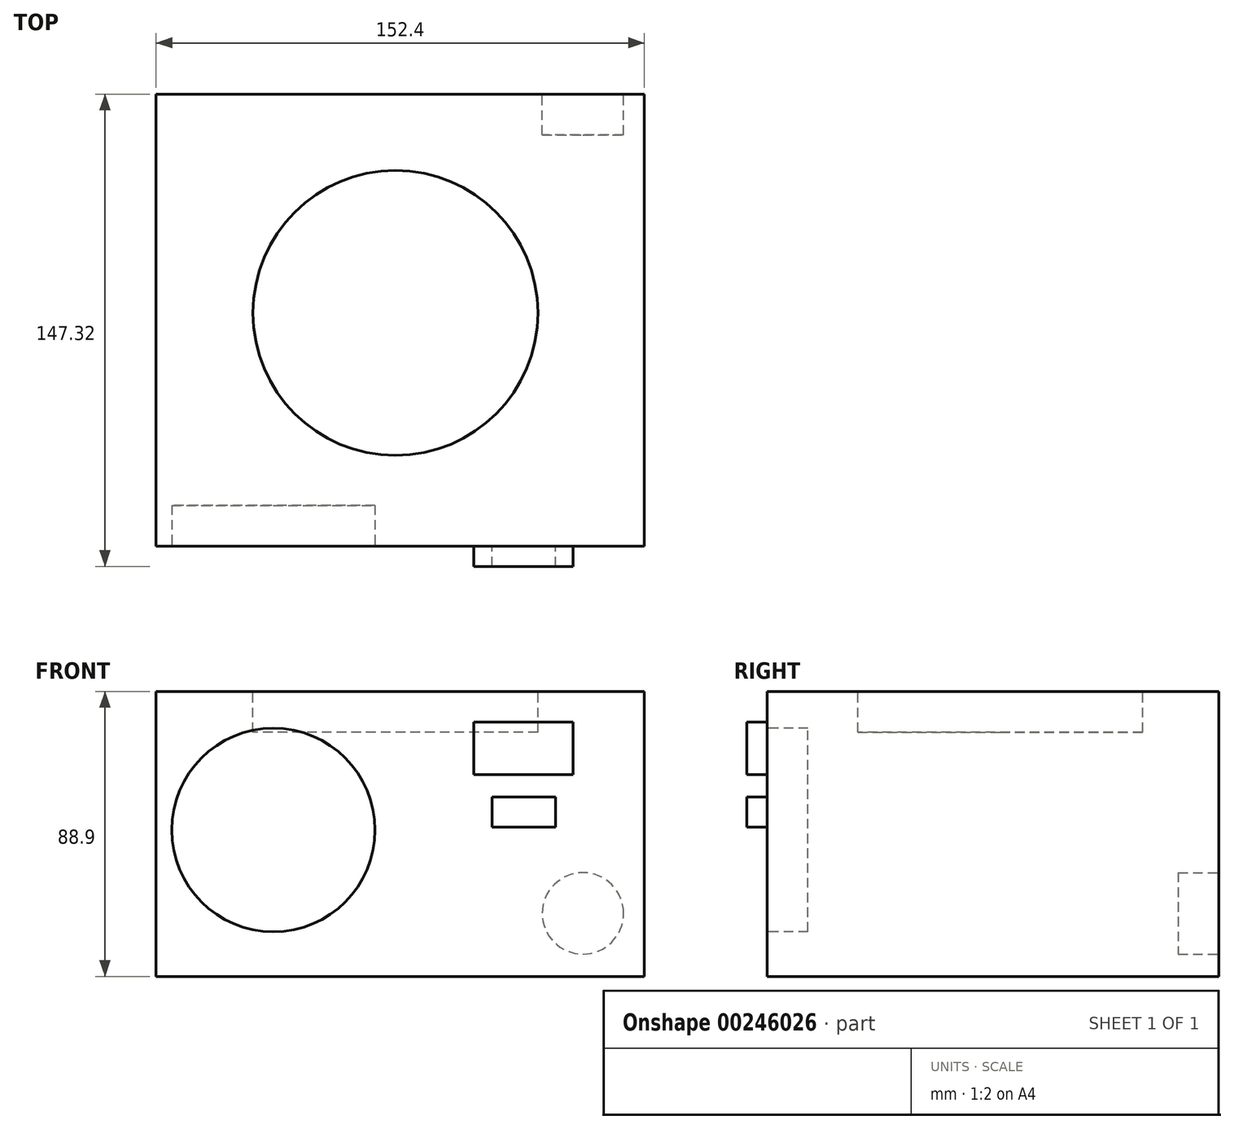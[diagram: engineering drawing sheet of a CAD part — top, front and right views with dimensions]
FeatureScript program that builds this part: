
annotation { "Feature Type Name" : "Feature", "Feature Type Description" : "" }
export const myFeature = defineFeature(function(context is Context, id is Id, definition is map)
    precondition{}
    {
        {
            var Q0;
            Q0=qCreatedBy(makeId("Front.planeOp"),FACE);
            var sketch = newSketch(context, id + "F0", { "sketchPlane" : qUnion([Q0])});
            skLineSegment(sketch, "E0.bottom", {"start": v(0, 0) * mm, "end": v(152.4, 0) * mm});
            skLineSegment(sketch, "E0.top", {"start": v(0, 88.9) * mm, "end": v(152.4, 88.9) * mm});
            skLineSegment(sketch, "E0.left", {"start": v(0, 0) * mm, "end": v(0, 88.9) * mm});
            skLineSegment(sketch, "E0.right", {"start": v(152.4, 0) * mm, "end": v(152.4, 88.9) * mm});
            skSolve(sketch);
        }
        {
            var Q0;
            Q0=makeQuery(id+"F0.imprint","IMPRINT",FACE,{"disambiguationData":[TD([[makeQuery(id+"F0.imprint","IMPRINT",EDGE,{"derivedFrom":sQuery(id+"F0.wireOp",EDGE,"E0.bottom")}),1.0]])]});
            extrude(context, id + "F1", {"entities" : qUnion([Q0]), "oppositeDirection" : true, "depth" : 140.97 * mm});
        }
        {
            var Q0;
            Q0=makeQuery(id+"F1.opExtrude","CAP_FACE",FACE,{"disambiguationData":[OSD([sQuery(id+"F0.wireOp",EDGE,"E0.bottom"),sQuery(id+"F0.wireOp",EDGE,"E0.top"),sQuery(id+"F0.wireOp",EDGE,"E0.left"),sQuery(id+"F0.wireOp",EDGE,"E0.right")])],"isStart":false});
            var sketch = newSketch(context, id + "F2", { "sketchPlane" : qUnion([Q0])});
            skCircle(sketch, "E1", {"center": v(-133.2, 19.65) * mm, "radius": 12.7 * mm});
            skSolve(sketch);
        }
        {
            var Q0;
            Q0=makeQuery(id+"F2.imprint","IMPRINT",FACE,{"disambiguationData":[TD([[makeQuery(id+"F2.imprint","IMPRINT",EDGE,{"derivedFrom":sQuery(id+"F2.wireOp",EDGE,"E1")}),1.0]])]});
            extrude(context, id + "F3", {"entities" : qUnion([Q0]), "operationType" : NewBodyOperationType.REMOVE, "oppositeDirection" : true, "depth" : 12.7 * mm});
        }
        {
            var Q0;
            Q0=makeQuery(id+"F1.opExtrude","SWEPT_FACE",FACE,{"disambiguationData":[OSD([sQuery(id+"F0.wireOp",EDGE,"E0.top")])]});
            var sketch = newSketch(context, id + "F4", { "sketchPlane" : qUnion([Q0])});
            skCircle(sketch, "E2", {"center": v(74.68, 72.68) * mm, "radius": 44.45 * mm});
            skSolve(sketch);
        }
        {
            var Q0;
            Q0=makeQuery(id+"F4.imprint","IMPRINT",FACE,{"disambiguationData":[TD([[makeQuery(id+"F4.imprint","IMPRINT",EDGE,{"derivedFrom":sQuery(id+"F4.wireOp",EDGE,"E2")}),1.0]])]});
            extrude(context, id + "F5", {"entities" : qUnion([Q0]), "operationType" : NewBodyOperationType.REMOVE, "oppositeDirection" : true, "depth" : 12.7 * mm});
        }
        {
            var Q0;
            Q0=makeQuery(id+"F1.opExtrude","CAP_FACE",FACE,{"disambiguationData":[OSD([sQuery(id+"F0.wireOp",EDGE,"E0.bottom"),sQuery(id+"F0.wireOp",EDGE,"E0.top"),sQuery(id+"F0.wireOp",EDGE,"E0.left"),sQuery(id+"F0.wireOp",EDGE,"E0.right")])],"isStart":true});
            var sketch = newSketch(context, id + "F6", { "sketchPlane" : qUnion([Q0])});
            skCircle(sketch, "E3", {"center": v(36.58, 45.67) * mm, "radius": 31.75 * mm});
            skLineSegment(sketch, "E4.bottom", {"start": v(99.12, 79.37) * mm, "end": v(130.1, 79.37) * mm});
            skLineSegment(sketch, "E4.top", {"start": v(99.12, 62.97) * mm, "end": v(130.1, 62.97) * mm});
            skLineSegment(sketch, "E4.left", {"start": v(99.12, 79.37) * mm, "end": v(99.12, 62.97) * mm});
            skLineSegment(sketch, "E4.right", {"start": v(130.1, 79.37) * mm, "end": v(130.1, 62.97) * mm});
            skLineSegment(sketch, "E5.bottom", {"start": v(104.9, 55.99) * mm, "end": v(124.63, 55.99) * mm});
            skLineSegment(sketch, "E5.top", {"start": v(104.9, 46.58) * mm, "end": v(124.63, 46.58) * mm});
            skLineSegment(sketch, "E5.left", {"start": v(104.9, 55.99) * mm, "end": v(104.9, 46.58) * mm});
            skLineSegment(sketch, "E5.right", {"start": v(124.63, 55.99) * mm, "end": v(124.63, 46.58) * mm});
            skSolve(sketch);
        }
        {
            var Q0;
            Q0=makeQuery(id+"F6.imprint","IMPRINT",FACE,{"disambiguationData":[TD([[makeQuery(id+"F6.imprint","IMPRINT",EDGE,{"derivedFrom":sQuery(id+"F6.wireOp",EDGE,"E3")}),1.0]])]});
            extrude(context, id + "F7", {"entities" : qUnion([Q0]), "operationType" : NewBodyOperationType.REMOVE, "oppositeDirection" : true, "depth" : 12.7 * mm});
        }
        {
            var Q0;
            Q0=makeQuery(id+"F6.imprint","IMPRINT",FACE,{"disambiguationData":[TD([[makeQuery(id+"F6.imprint","IMPRINT",EDGE,{"derivedFrom":sQuery(id+"F6.wireOp",EDGE,"E4.bottom")}),-1.0]])]});
            var Q1;
            Q1=makeQuery(id+"F6.imprint","IMPRINT",FACE,{"disambiguationData":[TD([[makeQuery(id+"F6.imprint","IMPRINT",EDGE,{"derivedFrom":sQuery(id+"F6.wireOp",EDGE,"E5.bottom")}),-1.0]])]});
            extrude(context, id + "F8", {"entities" : qUnion([Q0, Q1]), "operationType" : NewBodyOperationType.ADD, "depth" : 6.35 * mm});
        }
    });
